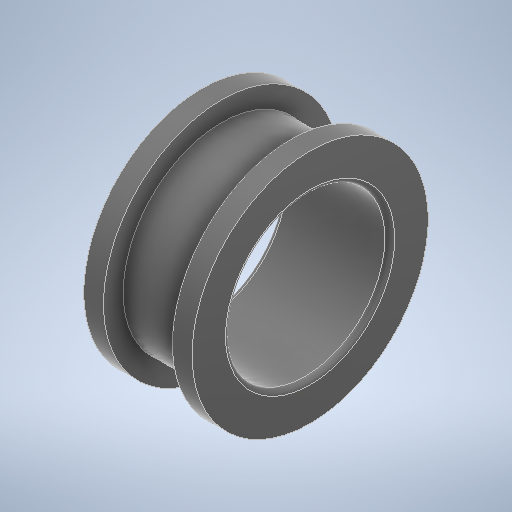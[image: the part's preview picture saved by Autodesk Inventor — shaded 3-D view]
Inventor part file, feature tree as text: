
AUTODESK INVENTOR PART (.ipt)
format: ipt  version: 2025.1 (Build 291241020, 241B)  size: 288,768 bytes
history: native  units: mm
features: revolve x1, mirror x1, fillet x1, sketch x1
ambient origin geometry x8: Origin, YZ Plane, XZ Plane, XY Plane, X Axis, Y Axis, Z Axis, Center Point
bodies: Solid1 (feature_tree)
feature tree (4):
  revolve  "Revolution1"  [1 undecoded]
  mirror  "Mirror2"
  fillet  "Fillet1"  Radius=10.0mm
  sketch  "Sketch1"  dims[d0=5.5mm d1=3.5mm d2=10.0mm d3=12.0mm d4=8.1mm d5=360.0deg d8=1.0mm d9=0.5mm]
note: 1 required parameter value undecoded (feature->parameter linkage not recoverable at this tier; creation-order binding heuristic only, values carry confidence <= 0.55)
